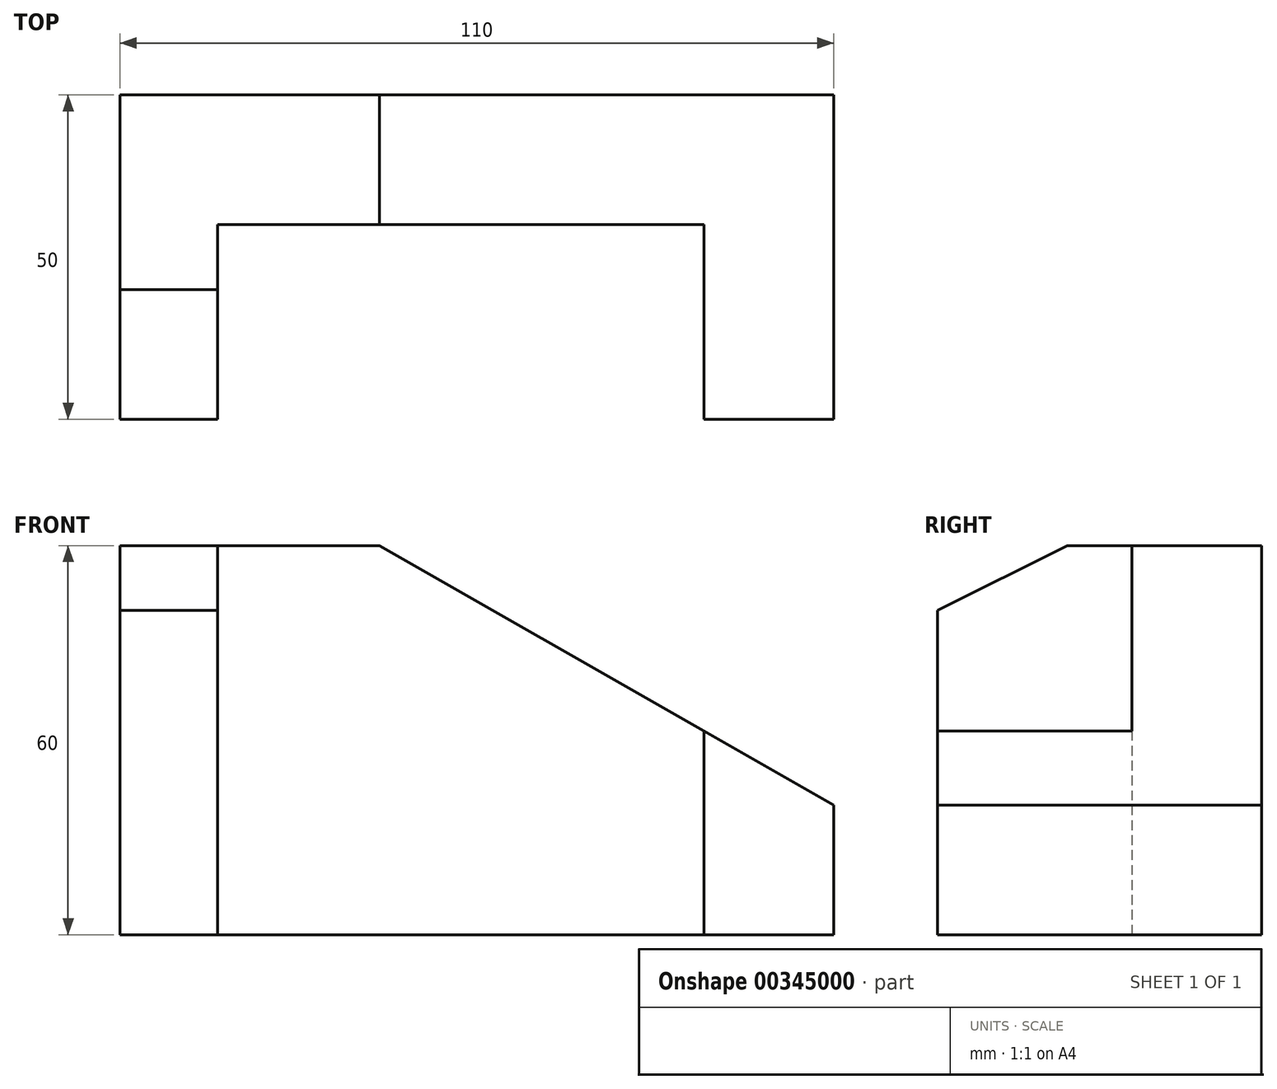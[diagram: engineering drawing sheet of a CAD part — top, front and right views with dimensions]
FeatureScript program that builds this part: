
annotation { "Feature Type Name" : "Feature", "Feature Type Description" : "" }
export const myFeature = defineFeature(function(context is Context, id is Id, definition is map)
    precondition{}
    {
        {
            var Q0;
            Q0=qCreatedBy(makeId("Top.planeOp"),FACE);
            var sketch = newSketch(context, id + "F0", { "sketchPlane" : qUnion([Q0])});
            skLineSegment(sketch, "E0.bottom", {"start": v(55, -25) * mm, "end": v(35, -25) * mm});
            skLineSegment(sketch, "E0.top", {"start": v(55, 25) * mm, "end": v(-55, 25) * mm});
            skLineSegment(sketch, "E0.left", {"start": v(55, -25) * mm, "end": v(55, 25) * mm});
            skLineSegment(sketch, "E0.right", {"start": v(-55, -25) * mm, "end": v(-55, 25) * mm});
            skPoint(sketch, "E0.middle", {"position": v(0, 0) * mm});
            skLineSegment(sketch, "E1", {"start": v(35, 5) * mm, "end": v(35, -25) * mm});
            skLineSegment(sketch, "E2", {"start": v(35, -25) * mm, "end": v(55, -25) * mm});
            skLineSegment(sketch, "E3", {"start": v(-40, -25) * mm, "end": v(-55, -25) * mm});
            skLineSegment(sketch, "E4", {"start": v(35, 5) * mm, "end": v(-40, 5) * mm});
            skLineSegment(sketch, "E5", {"start": v(-40, -25) * mm, "end": v(-40, 5) * mm});
            skSolve(sketch);
        }
        {
            var Q0;
            Q0=makeQuery(id+"F0.imprint","IMPRINT",FACE,{"disambiguationData":[TD([[makeQuery(id+"F0.imprint","IMPRINT",EDGE,{"derivedFrom":sQuery(id+"F0.wireOp",EDGE,"E0.top")}),1.0]])]});
            extrude(context, id + "F1", {"entities" : qUnion([Q0]), "depth" : 60 * mm});
        }
        {
            var Q0;
            Q0=makeQuery(id+"F1.opExtrude","SWEPT_FACE",FACE,{"disambiguationData":[OSD([sQuery(id+"F0.wireOp",EDGE,"E0.right")])]});
            var sketch = newSketch(context, id + "F2", { "sketchPlane" : qUnion([Q0])});
            skLineSegment(sketch, "E6", {"start": v(25, 60) * mm, "end": v(5, 60) * mm});
            skLineSegment(sketch, "E7", {"start": v(25, 60) * mm, "end": v(25, 50) * mm});
            skLineSegment(sketch, "E8", {"start": v(25, 50) * mm, "end": v(5, 60) * mm});
            skSolve(sketch);
        }
        {
            var Q0;
            Q0=makeQuery(id+"F2.imprint","IMPRINT",FACE,{"disambiguationData":[TD([[makeQuery(id+"F2.imprint","IMPRINT",EDGE,{"derivedFrom":sQuery(id+"F2.wireOp",EDGE,"E6")}),1.0]])]});
            extrude(context, id + "F3", {"entities" : qUnion([Q0]), "operationType" : NewBodyOperationType.REMOVE, "oppositeDirection" : true, "depth" : 25 * mm});
        }
        {
            var Q0;
            Q0=makeQuery(id+"F1.opExtrude","SWEPT_FACE",FACE,{"disambiguationData":[OSD([sQuery(id+"F0.wireOp",EDGE,"E0.top")])]});
            var sketch = newSketch(context, id + "F4", { "sketchPlane" : qUnion([Q0])});
            skLineSegment(sketch, "E9", {"start": v(-55, 0) * mm, "end": v(-55, 20) * mm});
            skLineSegment(sketch, "E10", {"start": v(55, 60) * mm, "end": v(15, 60) * mm});
            skLineSegment(sketch, "E11", {"start": v(-55, 20) * mm, "end": v(15, 60) * mm});
            skLineSegment(sketch, "E12.0", {"start": v(-55, 60) * mm, "end": v(55, 60) * mm});
            skLineSegment(sketch, "E13.0", {"start": v(-55, 60) * mm, "end": v(-55, 0) * mm});
            skSolve(sketch);
        }
        {
            var Q0;
            {var subQ0=sQuery(id+"F4.wireOp",EDGE,"E11");Q0=makeQuery(id+"F4.imprint","IMPRINT",FACE,{"disambiguationData":[TD([[makeQuery(id+"F4.imprint","IMPRINT",EDGE,{"derivedFrom":subQ0}),1.0]])]});}
            extrude(context, id + "F5", {"entities" : qUnion([Q0]), "operationType" : NewBodyOperationType.REMOVE, "oppositeDirection" : true, "depth" : 60 * mm});
        }
    });
